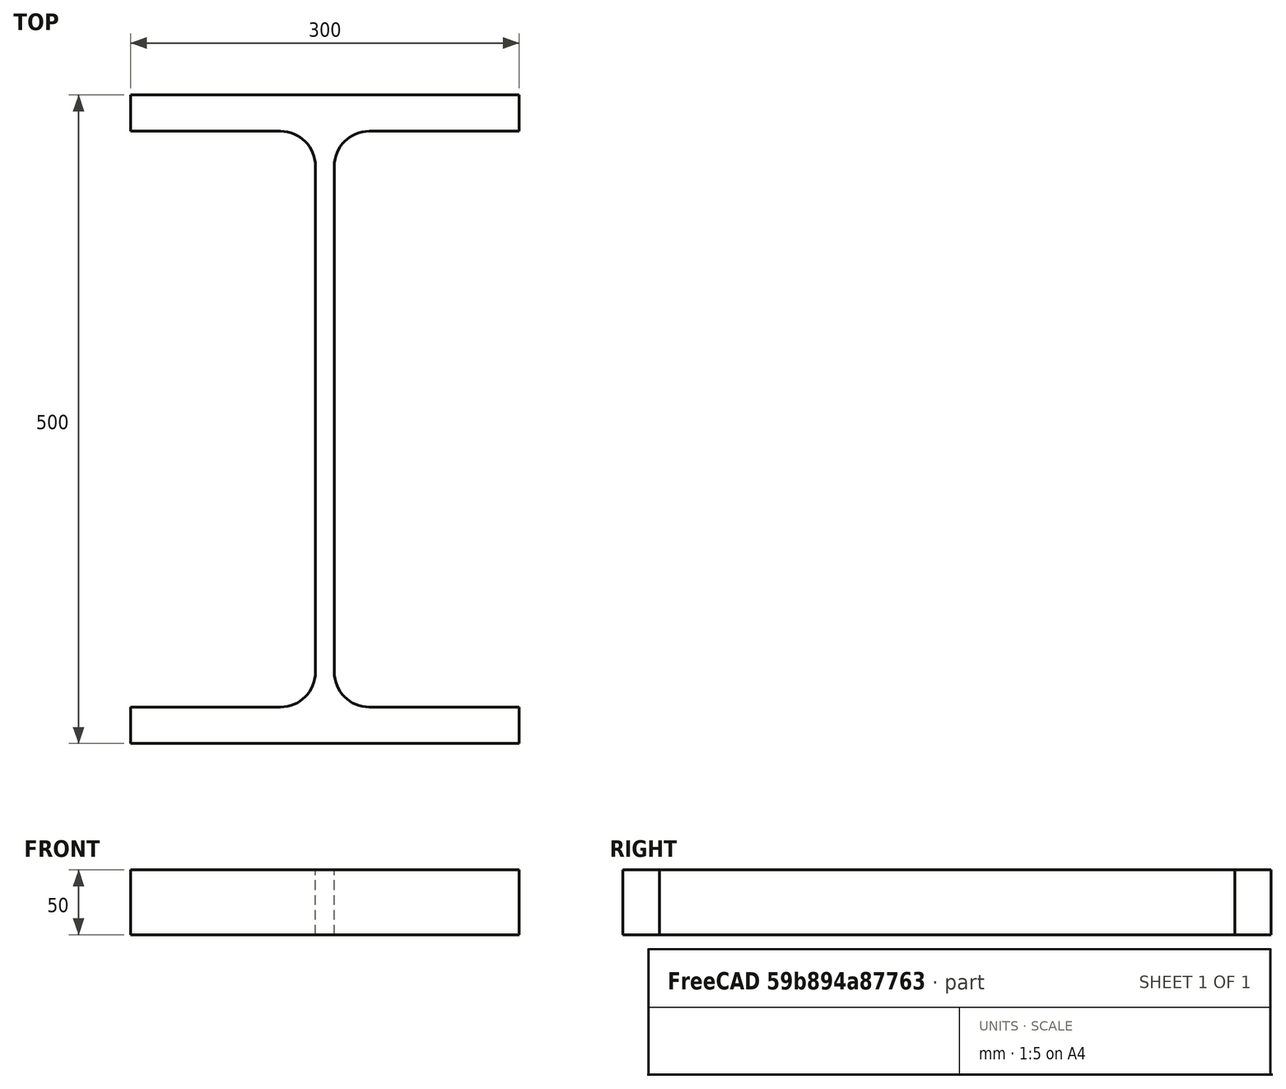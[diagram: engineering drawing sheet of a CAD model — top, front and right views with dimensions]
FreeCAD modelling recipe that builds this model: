
FCSTD DOCUMENT  (FreeCAD 0.15R4671 (Git))
Label: HE-B-Profile 500 DIN1025-2 S235JR
License: All rights reserved
LicenseURL: http://en.wikipedia.org/wiki/All_rights_reserved
objects: Sketcher::SketchObject×1, Part::Extrusion×1
note: 2 computed .brp shape members not serialized (recipe doc carries the construction recipe); baked Part::Feature solids carry a one-line shape summary decoded from their .brp

FEATURE [Sketcher::SketchObject] Sketch
  sketch-geometry (16):
    g0: LineSegment StartX=7.25 StartY=-195 StartZ=0 EndX=7.25 EndY=195 EndZ=0
    g1: LineSegment StartX=34.25 StartY=222 StartZ=0 EndX=150 EndY=222 EndZ=0
    g2: LineSegment StartX=150 StartY=222 StartZ=0 EndX=150 EndY=250 EndZ=0
    g3: LineSegment StartX=150 StartY=250 StartZ=0 EndX=-150 EndY=250 EndZ=0
    g4: LineSegment StartX=-150 StartY=250 StartZ=0 EndX=-150 EndY=222 EndZ=0
    g5: LineSegment StartX=-150 StartY=222 StartZ=0 EndX=-34.25 EndY=222 EndZ=0
    g6: LineSegment StartX=-7.25 StartY=195 StartZ=0 EndX=-7.25 EndY=-195 EndZ=0
    g7: LineSegment StartX=-34.25 StartY=-222 StartZ=0 EndX=-150 EndY=-222 EndZ=0
    g8: LineSegment StartX=-150 StartY=-222 StartZ=0 EndX=-150 EndY=-250 EndZ=0
    g9: LineSegment StartX=-150 StartY=-250 StartZ=0 EndX=150 EndY=-250 EndZ=0
    g10: LineSegment StartX=150 StartY=-250 StartZ=0 EndX=150 EndY=-222 EndZ=0
    g11: LineSegment StartX=150 StartY=-222 StartZ=0 EndX=34.25 EndY=-222 EndZ=0
    g12: ArcOfCircle CenterX=34.25 CenterY=195 CenterZ=0 NormalX=0 NormalY=0 NormalZ=1 Radius=27 StartAngle=1.5708 EndAngle=3.14159
    g13: ArcOfCircle CenterX=34.25 CenterY=-195 CenterZ=0 NormalX=0 NormalY=0 NormalZ=1 Radius=27 StartAngle=3.14159 EndAngle=4.71239
    g14: ArcOfCircle CenterX=-34.25 CenterY=195 CenterZ=0 NormalX=0 NormalY=0 NormalZ=1 Radius=27 StartAngle=0 EndAngle=1.5708
    g15: ArcOfCircle CenterX=-34.25 CenterY=-195 CenterZ=0 NormalX=0 NormalY=0 NormalZ=1 Radius=27 StartAngle=4.71239 EndAngle=6.28319
  constraints (42):
    c: Vertical(g0)
    c: Coincident(g2,g1)
    c: Vertical(g2)
    c: Coincident(g3,g2)
    c: Coincident(g4,g3)
    c: Vertical(g4)
    c: Coincident(g5,g4)
    c: Horizontal(g5)
    c: Vertical(g6)
    c: Horizontal(g7)
    c: Coincident(g8,g7)
    c: Vertical(g8)
    c: Coincident(g9,g8)
    c: Horizontal(g9)
    c: Coincident(g10,g9)
    c: Vertical(g10)
    c: Coincident(g11,g10)
    c: Horizontal(g11)
    c: Tangent(g1,g12) = 1.5708
    c: Tangent(g0,g12) = 1.5708
    c: Tangent(g0,g13) = 1.5708
    c: Tangent(g11,g13) = 1.5708
    c: Tangent(g5,g14) = 1.5708
    c: Tangent(g6,g14) = 1.5708
    c: Tangent(g6,g15) = 1.5708
    c: Tangent(g7,g15) = 1.5708
    c: Equal(g3,g9)
    c: Equal(g2,g4)
    c: Equal(g4,g8)
    c: Equal(g8,g10)
    c: Equal(g12,g14)
    c: Equal(g14,g15)
    c: Equal(g15,g13)
    c: Symmetric(g2,g3,g-2)
    c: Symmetric(g9,g8,g-2)
    c: Symmetric(g0,g6,g-2)
    c: Symmetric(g2,g9,g-1)
    c: DistanceY(g2,g9) = -500
    c: DistanceX(g3) = -300
    c: DistanceX(g0,g6) = -14.5
    c: DistanceY(g2) = 28
    c: Radius(g12) = 27
FEATURE [Part::Extrusion] Extrude  label="HE-B-Profile 500 DIN1025-2 S235JR"
  Base = -> Sketch
  Dir = (0,0,50)
  Solid = true
